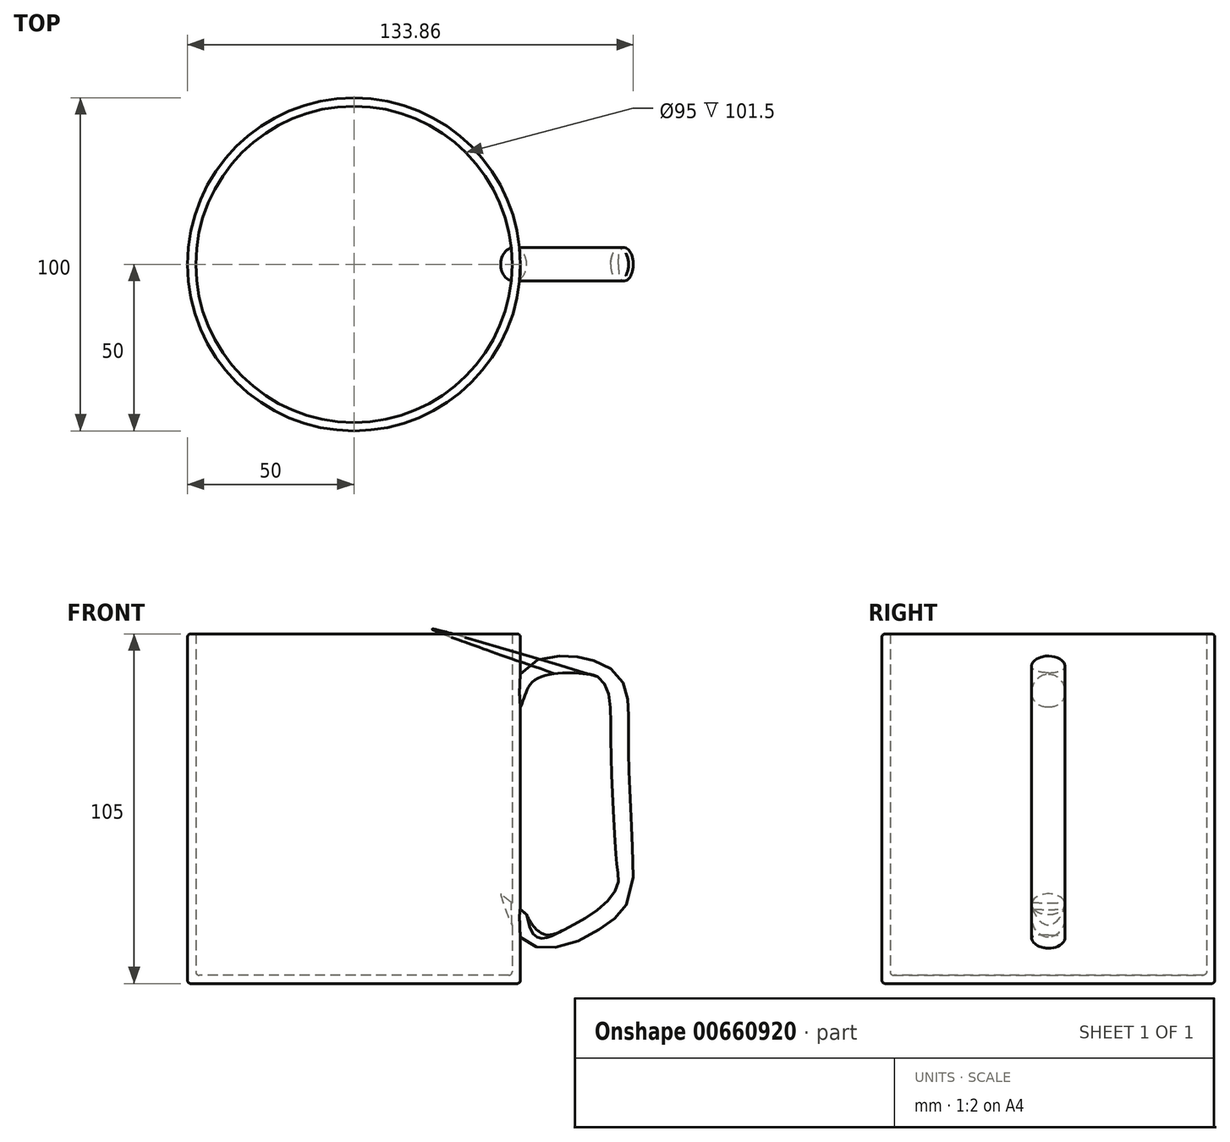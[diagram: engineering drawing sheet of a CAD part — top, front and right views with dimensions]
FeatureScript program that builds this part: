
annotation { "Feature Type Name" : "Feature", "Feature Type Description" : "" }
export const myFeature = defineFeature(function(context is Context, id is Id, definition is map)
    precondition{}
    {
        {
            var Q0;
            Q0=qCreatedBy(makeId("Top.planeOp"),FACE);
            var sketch = newSketch(context, id + "F0", { "sketchPlane" : qUnion([Q0])});
            skCircle(sketch, "E0", {"center": v(0, 0) * mm, "radius": 50 * mm});
            skSolve(sketch);
        }
        {
            var Q0;
            Q0=makeQuery(id+"F0.imprint","IMPRINT",FACE,{"disambiguationData":[TD([[makeQuery(id+"F0.imprint","IMPRINT",EDGE,{"derivedFrom":sQuery(id+"F0.wireOp",EDGE,"E0")}),1.0]])]});
            extrude(context, id + "F1", {"entities" : qUnion([Q0]), "depth" : 105 * mm, "offsetDistance" : 25 * mm});
        }
        {
            var Q0;
            Q0=qCreatedBy(makeId("Front.planeOp"),FACE);
            var sketch = newSketch(context, id + "F2", { "sketchPlane" : qUnion([Q0])});
            skFitSpline(sketch, "E1", {"points": [v(49.46, 87.57) * mm, v(58, 95.09) * mm, v(75.93, 91.96) * mm, v(80.04, 72.68) * mm, v(81.42, 36.93) * mm, v(77.7, 22.84) * mm, v(56.46, 13.54) * mm, v(47.56, 24.15) * mm], "startDerivative": vector(60.25, 104.12) * mm, "endDerivative": vector(-40.45, 111.39) * mm});
            skSolve(sketch);
        }
        {
            var Q0;
            Q0=qCreatedBy(makeId("Right.planeOp"),FACE);
            cPlane(context, id + "F3", {"entities" : qUnion([Q0]), "cplaneType" : CPlaneType.OFFSET, "offset" : 50 * mm, "width" : 150 * mm, "height" : 150 * mm});
        }
        {
            var Q0;
            Q0=makeQuery(id+"F1.opExtrude","CAP_FACE",FACE,{"disambiguationData":[OSD([sQuery(id+"F0.wireOp",EDGE,"E0")])],"isStart":false});
            shell(context, id + "F4", {"entities" : qUnion([Q0]), "thickness" : 2.5 * mm});
        }
        {
            var Q0;
            Q0=qCreatedBy(id+"F3.planeOp",FACE);
            var sketch = newSketch(context, id + "F5", { "sketchPlane" : qUnion([Q0])});
            skCircle(sketch, "E2", {"center": v(0, 87.97) * mm, "radius": 5 * mm});
            skSolve(sketch);
        }
        {
            var Q0;
            Q0=makeQuery(id+"F5.imprint","IMPRINT",FACE,{"disambiguationData":[TD([[makeQuery(id+"F5.imprint","IMPRINT",EDGE,{"derivedFrom":sQuery(id+"F5.wireOp",EDGE,"E2")}),1.0]])]});
            var Q1;
            Q1=sQuery(id+"F2.wireOp",EDGE,"E1");
            sweep(context, id + "F6", {"operationType" : NewBodyOperationType.ADD, "profiles" : qUnion([Q0]), "path" : qUnion([Q1])});
        }
        {
            var Q0;
            {var subQ0=sQuery(id+"F0.wireOp",EDGE,"E0");Q0=makeQuery(id+"F4.opShell","OFFSET_EDGE",EDGE,{"disambiguationData":[OSD([subQ0]),TDD([makeQuery(id+"F1.opExtrude","CAP_EDGE",EDGE,{"disambiguationData":[OSD([subQ0])],"isStart":true})])]});}
            var Q1;
            Q1=makeQuery(id+"F1.opExtrude","CAP_EDGE",EDGE,{"disambiguationData":[OSD([sQuery(id+"F0.wireOp",EDGE,"E0")])],"isStart":false});
            var Q2;
            Q2=makeQuery(id+"F1.opExtrude","CAP_EDGE",EDGE,{"disambiguationData":[OSD([sQuery(id+"F0.wireOp",EDGE,"E0")])],"isStart":true});
            fillet(context, id + "F7", {"entities" : qUnion([Q0, Q1, Q2]), "radius" : 1 * mm, "tangentPropagation" : true, "allowEdgeOverflow" : false});
        }
    });
